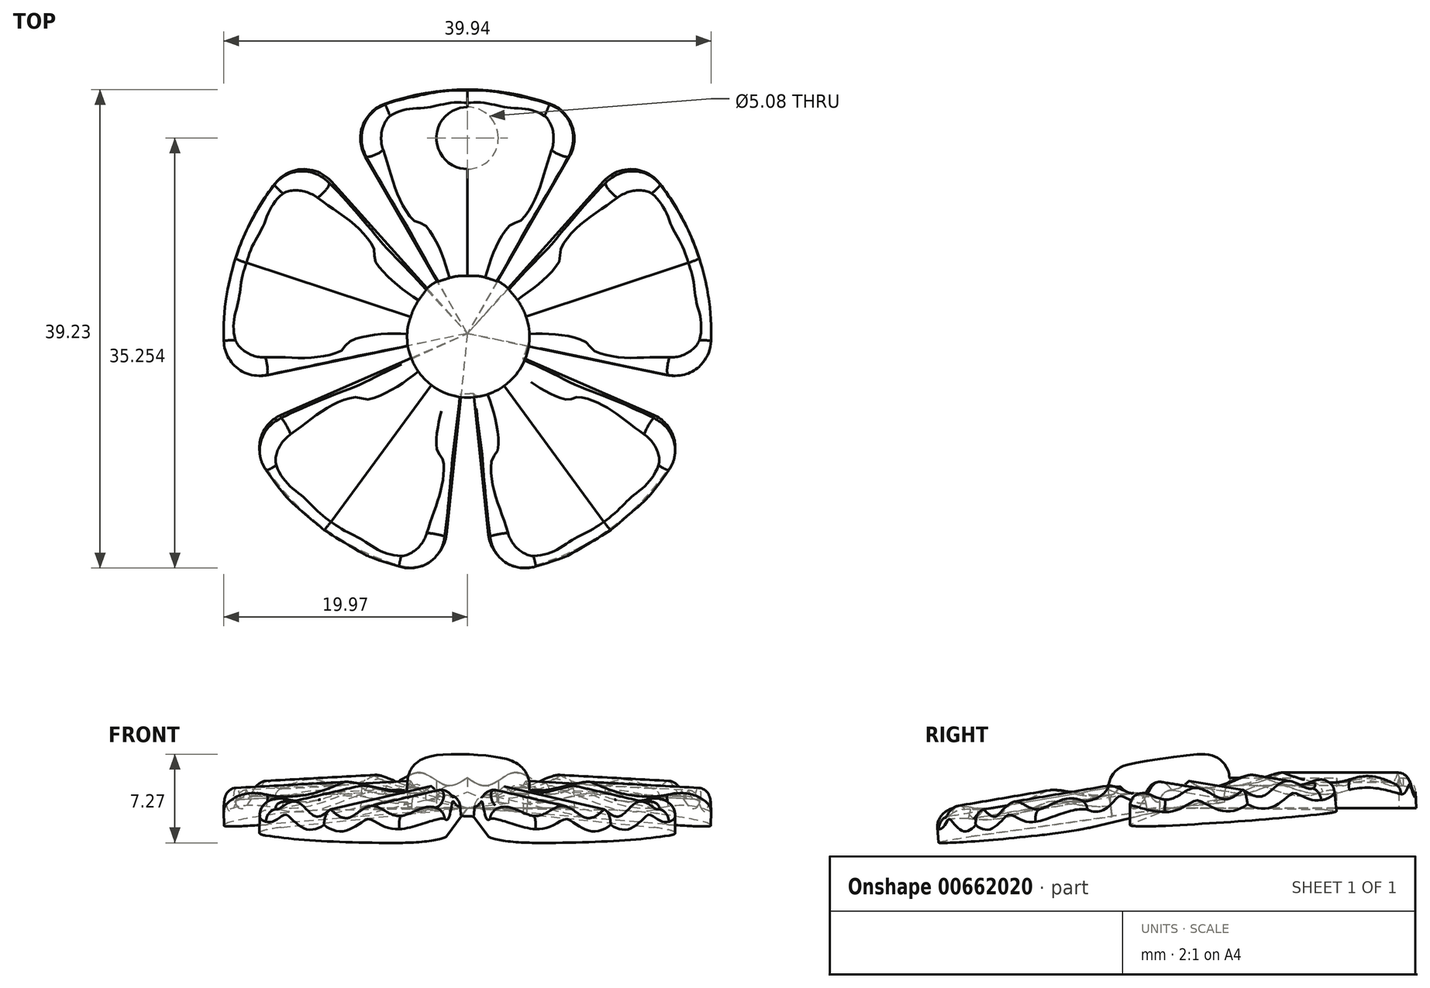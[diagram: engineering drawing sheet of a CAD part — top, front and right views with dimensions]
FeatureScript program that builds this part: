
annotation { "Feature Type Name" : "Feature", "Feature Type Description" : "" }
export const myFeature = defineFeature(function(context is Context, id is Id, definition is map)
    precondition{}
    {
        {
            var Q0;
            Q0=qCreatedBy(makeId("Top.planeOp"),FACE);
            var sketch = newSketch(context, id + "F0", { "sketchPlane" : qUnion([Q0])});
            skArc(sketch, "E0", {"start": v(6.79, -1.19) * mm, "mid": v(0, 0) * mm, "end": v(-6.79, -1.19) * mm});
            skLineSegment(sketch, "E1", {"start": v(-8.37, -5.5) * mm, "end": v(0, -20) * mm});
            skLineSegment(sketch, "E2", {"start": v(0, -20) * mm, "end": v(8.37, -5.5) * mm});
            skPoint(sketch, "E3.visualSharp", {"position": v(-10, -2.68) * mm});
            skArc(sketch, "E3.filletArc", {"start": v(-6.79, -1.19) * mm, "mid": v(-8.59, -2.98) * mm, "end": v(-8.37, -5.5) * mm});
            skPoint(sketch, "E4.visualSharp", {"position": v(10, -2.68) * mm});
            skArc(sketch, "E4.filletArc", {"start": v(8.37, -5.5) * mm, "mid": v(8.59, -2.98) * mm, "end": v(6.79, -1.19) * mm});
            skSolve(sketch);
        }
        {
            var Q0;
            Q0=qCreatedBy(makeId("Right.planeOp"),FACE);
            var sketch = newSketch(context, id + "F1", { "sketchPlane" : qUnion([Q0])});
            skLineSegment(sketch, "E5", {"start": v(-20, 0) * mm, "end": v(-20.55, 7.29) * mm, "construction": true});
            skSolve(sketch);
        }
        {
            var Q0;
            Q0=makeQuery(id+"F0.imprint","IMPRINT",FACE,{"disambiguationData":[TD([[makeQuery(id+"F0.imprint","IMPRINT",EDGE,{"derivedFrom":sQuery(id+"F0.wireOp",EDGE,"E0")}),1.0]])]});
            extrude(context, id + "F2", {"entities" : qUnion([Q0]), "depth" : 5 * mm, "offsetDistance" : 25.4 * mm, "hasDraft" : true, "draftAngle" : 3 * degree, "draftPullDirection" : true});
        }
        {
            var Q0;
            Q0=qCreatedBy(makeId("Front.planeOp"),FACE);
            var sketch = newSketch(context, id + "F3", { "sketchPlane" : qUnion([Q0])});
            skLineSegment(sketch, "E6", {"start": v(0, 2.47) * mm, "end": v(0, 6.34) * mm});
            skLineSegment(sketch, "E7", {"start": v(0, 6.34) * mm, "end": v(8.56, 6.34) * mm});
            skFitSpline(sketch, "E8", {"points": [v(8.56, 6.34) * mm, v(7.88, 3.43) * mm, v(6.17, 2.07) * mm, v(3.94, 2.9) * mm, v(1.73, 1.85) * mm, v(0, 2.47) * mm], "startDerivative": vector(-1.5, -13.53) * mm, "endDerivative": vector(-9.55, 6.54) * mm});
            skLineSegment(sketch, "E9.MirrorCS", {"start": v(0, 6.34) * mm, "end": v(-8.56, 6.34) * mm});
            skFitSpline(sketch, "E10.MirrorCS", {"points": [v(-8.56, 6.34) * mm, v(-7.88, 3.43) * mm, v(-6.17, 2.07) * mm, v(-3.94, 2.9) * mm, v(-1.73, 1.85) * mm, v(0, 2.47) * mm], "startDerivative": vector(1.5, -13.53) * mm, "endDerivative": vector(9.55, 6.54) * mm});
            skSolve(sketch);
        }
        {
            var Q0;
            Q0 = qSketchRegion(id + "F3", true);
            extrude(context, id + "F4", {"entities" : qUnion([Q0]), "operationType" : NewBodyOperationType.REMOVE, "depth" : 25.4 * mm, "offsetDistance" : 25.4 * mm});
        }
        {
            var Q0;
            Q0=makeQuery(id+"F4.boolean.opBoolean","INTERSECT",EDGE,{"derivedFrom":[makeQuery(id+"F2.opExtrude","SWEPT_FACE",FACE,{"disambiguationData":[OSD([sQuery(id+"F0.wireOp",EDGE,"E2")])]}),makeQuery(id+"F4.opExtrude","SWEPT_FACE",FACE,{"disambiguationData":[OSD([sQuery(id+"F3.wireOp",EDGE,"E8")])]})]});
            var Q1;
            Q1=makeQuery(id+"F4.boolean.opBoolean","INTERSECT",EDGE,{"derivedFrom":[makeQuery(id+"F2.opExtrude","SWEPT_FACE",FACE,{"disambiguationData":[OSD([sQuery(id+"F0.wireOp",EDGE,"E1")])]}),makeQuery(id+"F4.opExtrude","SWEPT_FACE",FACE,{"disambiguationData":[OSD([sQuery(id+"F3.wireOp",EDGE,"E10.MirrorCS")])]})]});
            fillet(context, id + "F5", {"entities" : qUnion([Q0, Q1]), "radius" : 1 * mm, "tangentPropagation" : true, "allowEdgeOverflow" : false});
        }
        {
            var Q0;
            Q0=makeQuery(id+"F2.opExtrude","SWEPT_BODY",BODY,{"disambiguationData":[OSD([sQuery(id+"F0.wireOp",EDGE,"E0"),sQuery(id+"F0.wireOp",EDGE,"E1"),sQuery(id+"F0.wireOp",EDGE,"E2"),sQuery(id+"F0.wireOp",EDGE,"E3.filletArc"),sQuery(id+"F0.wireOp",EDGE,"E4.filletArc")])]});
            var Q1;
            Q1=sQuery(id+"F1.wireOp",EDGE,"E5");
            circularPattern(context, id + "F6", {"entities" : qUnion([Q0]), "axis" : qUnion([Q1]), "angle" : 360 * degree, "instanceCount" : 5, "equalSpace" : true});
        }
        {
            var Q0;
            Q0=makeQuery(id+"F6.opPattern","COPY",FACE,{"derivedFrom":makeQuery(id+"F2.opExtrude","CAP_FACE",FACE,{"disambiguationData":[OSD([sQuery(id+"F0.wireOp",EDGE,"E0"),sQuery(id+"F0.wireOp",EDGE,"E1"),sQuery(id+"F0.wireOp",EDGE,"E2"),sQuery(id+"F0.wireOp",EDGE,"E3.filletArc"),sQuery(id+"F0.wireOp",EDGE,"E4.filletArc")])],"isStart":true}),"instanceName":"3"});
            var sketch = newSketch(context, id + "F7", { "sketchPlane" : qUnion([Q0])});
            skCircle(sketch, "E11", {"center": v(-0.12, 19.81) * mm, "radius": 5 * mm});
            skSolve(sketch);
        }
        {
            var Q0;
            Q0 = qSketchRegion(id + "F7", true);
            extrude(context, id + "F8", {"entities" : qUnion([Q0]), "operationType" : NewBodyOperationType.ADD, "oppositeDirection" : true, "depth" : 4 * mm, "offsetDistance" : 25.4 * mm});
        }
        {
            var Q0;
            Q0=makeQuery(id+"F8.opExtrude","CAP_EDGE",EDGE,{"disambiguationData":[OSD([sQuery(id+"F7.wireOp",EDGE,"E11")])],"isStart":false});
            fillet(context, id + "F9", {"entities" : qUnion([Q0]), "radius" : 2 * mm, "tangentPropagation" : true, "allowEdgeOverflow" : false});
        }
        {
            var Q0;
            Q0=qCreatedBy(makeId("Top.planeOp"),FACE);
            var sketch = newSketch(context, id + "F10", { "sketchPlane" : qUnion([Q0])});
            skCircle(sketch, "E12", {"center": v(0, -3.98) * mm, "radius": 2.54 * mm});
            skSolve(sketch);
        }
        {
            var Q0;
            Q0 = qSketchRegion(id + "F10", true);
            extrude(context, id + "F11", {"entities" : qUnion([Q0]), "operationType" : NewBodyOperationType.REMOVE, "depth" : 25.4 * mm, "offsetDistance" : 25.4 * mm});
        }
    });
